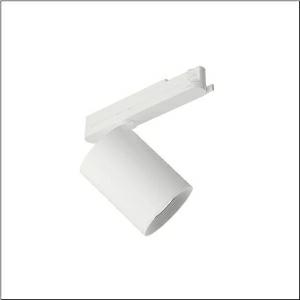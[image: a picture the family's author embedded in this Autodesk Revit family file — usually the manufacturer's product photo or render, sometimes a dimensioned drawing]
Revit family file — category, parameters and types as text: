
# Revit family: spot_21_51se13mbd5b
name_source: partatom
category: Lighting Fixtures
units: mm (PartAtom-declared; Revit-internal decimal feet)

## family parameters
Cut with Voids When Loaded = No
Host = Face
Light Source = No
Part Type = Normal
Room Calculation Point = No
Round Connector Dimension = Use Diameter
Shared = No

## types (1)
- --- (1 x LED, 5520 lm, 41.5 W, 4000K)
    Apparent Load = 42 VA
    CIE Flux Codes = 95 98 99 100 100
    Color Rendering = 90
    Color Temperature = 4000K
    Default Elevation = 1800 mm
    Description = Spot 21, directional spotlight, light control with lens, of PMMA, LED rated luminous flux: 5.300lm, light colour: 940, control gear: ECG Multilumen, with 3-phase adapter, mains connection: 220..240V, AC, 50/60Hz, of aluminium, traffic white (RAL 9016), length: 213mm, diameter: 105mm, protection rating (complete): IP20, insulation class (complete): insulation class I (protective earthing), certification: CE, impact resistance: IK02, permissible ambient temperature for indoor applications: -20..+40°C, packaging unit: 1 piece
    Height = 175 mm
    Lamp = 1 x LED
    Lamp Light Flux = 5520 lm
    Lamp Power = 41.5 W
    Lamp count = 1
    Length = 105 mm
    Luminous efficacy = 133 lm/W
    Manufacturer = Siteco
    ModVariant = No
    Model = 51SE13MBD5B
    Mounting Place = Ceiling
    Mounting Type = Pendant
    Number of Poles = 1
    OnlyDefault = Yes
    Power Factor = 1
    Product Name = Spot 21
    Product group = directional spotlight
    ProductGroupID = 905
    Protection Class = Protection class I
    Protection Degree = IP 20
    RLX_Detail_Level = 1
    RLX_Emergency_Light_Flux = 0 lm
    RLX_Emergency_Type = 0
    RLX_Emergency_Type_DB = No
    RlxData = <blob elided: 17609 chars, md5=1fe9bfde>
    Socket = socket
    Standby Power = 0 W
    System Light Flux = 5520 lm
    System Power = 42 W
    Type Comments = factory setting: luminous flux: 100 % | (ON | ON | ON | ON) | 1050 mA
    Type Image = l_1003976.jpg
    URL = http://relux.com
    VarID = @adj_165633
    Voltage = 0 V
    Weight = 0.00 kg
    Width = 0 mm  [stored 0 ft]

note: [stored X ft] marks values corroborated as IEEE doubles in the binary element streams (Revit-internal decimal feet)

## geometry (parser evidence)
native form markers: Blend x4, Sweep x10
no freeform markers — native parametric forms only
